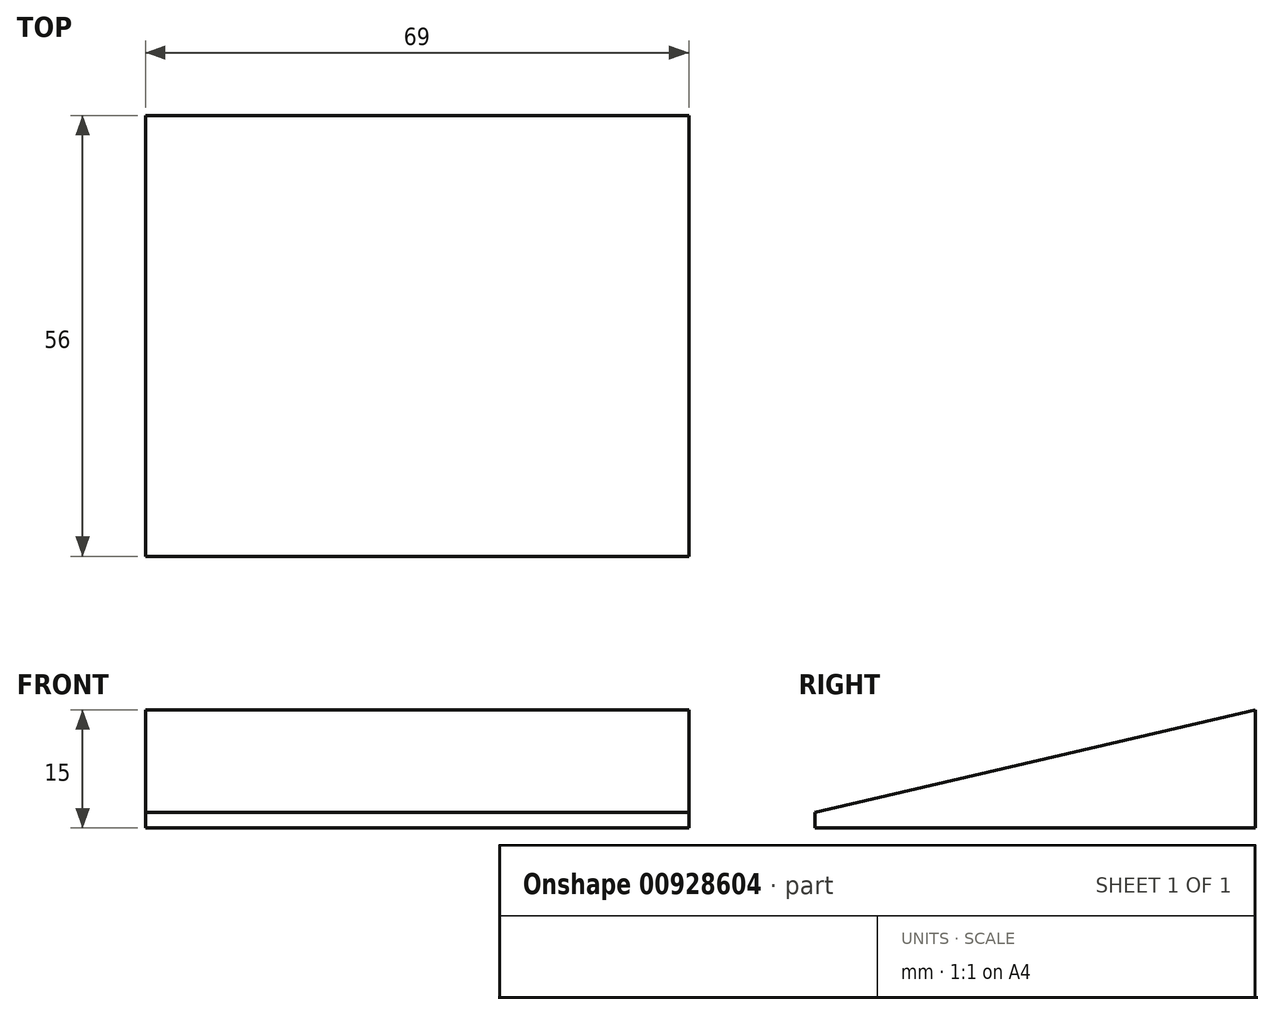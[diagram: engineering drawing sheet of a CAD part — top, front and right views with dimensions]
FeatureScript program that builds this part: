
annotation { "Feature Type Name" : "Feature", "Feature Type Description" : "" }
export const myFeature = defineFeature(function(context is Context, id is Id, definition is map)
    precondition{}
    {
        {
            var Q0;
            Q0=qCreatedBy(makeId("Right.planeOp"),FACE);
            var sketch = newSketch(context, id + "F0", { "sketchPlane" : qUnion([Q0])});
            skLineSegment(sketch, "E0", {"start": v(-22, 0) * mm, "end": v(34, 0) * mm});
            skLineSegment(sketch, "E1", {"start": v(34, 0) * mm, "end": v(34, 15) * mm});
            skLineSegment(sketch, "E2", {"start": v(34, 15) * mm, "end": v(-22, 2) * mm});
            skLineSegment(sketch, "E3", {"start": v(-22, 2) * mm, "end": v(-22, 0) * mm});
            skSolve(sketch);
        }
        {
            var Q0;
            Q0 = qSketchRegion(id + "F0", true);
            extrude(context, id + "F1", {"entities" : qUnion([Q0]), "depth" : 25 * mm, "offsetDistance" : 25 * mm});
        }
        {
            var Q0;
            Q0=makeQuery(id+"F1.opExtrude","CAP_FACE",FACE,{"disambiguationData":[OSD([sQuery(id+"F0.wireOp",EDGE,"E0"),sQuery(id+"F0.wireOp",EDGE,"E1"),sQuery(id+"F0.wireOp",EDGE,"E2"),sQuery(id+"F0.wireOp",EDGE,"E3")])],"isStart":false});
            extrude(context, id + "F2", {"entities" : qUnion([Q0]), "operationType" : NewBodyOperationType.ADD, "depth" : 44 * mm, "offsetDistance" : 25 * mm});
        }
    });
